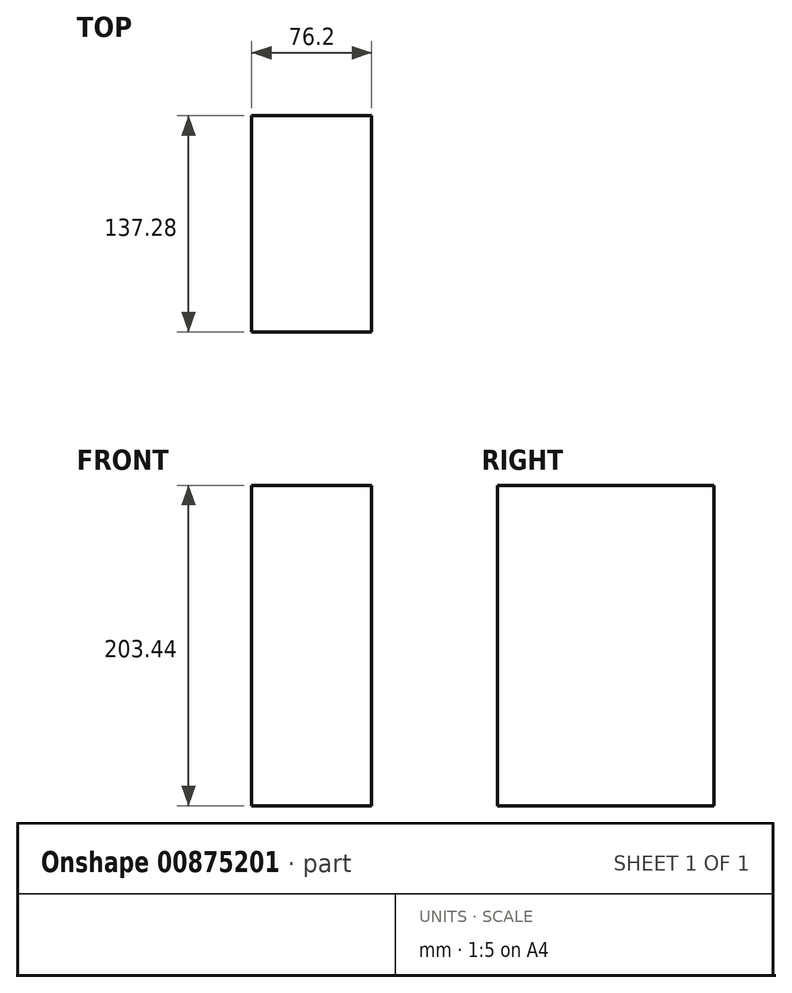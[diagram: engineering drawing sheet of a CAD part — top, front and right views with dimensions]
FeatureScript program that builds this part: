
annotation { "Feature Type Name" : "Feature", "Feature Type Description" : "" }
export const myFeature = defineFeature(function(context is Context, id is Id, definition is map)
    precondition{}
    {
        {
            var Q0;
            Q0=qCreatedBy(makeId("Right.planeOp"),FACE);
            var sketch = newSketch(context, id + "F0", { "sketchPlane" : qUnion([Q0])});
            skLineSegment(sketch, "E0.bottom", {"start": v(-68.64, 101.72) * mm, "end": v(68.64, 101.72) * mm});
            skLineSegment(sketch, "E0.top", {"start": v(-68.64, -101.72) * mm, "end": v(68.64, -101.72) * mm});
            skLineSegment(sketch, "E0.left", {"start": v(-68.64, 101.72) * mm, "end": v(-68.64, -101.72) * mm});
            skLineSegment(sketch, "E0.right", {"start": v(68.64, 101.72) * mm, "end": v(68.64, -101.72) * mm});
            skPoint(sketch, "E0.middle", {"position": v(0, 0) * mm});
            skSolve(sketch);
        }
        {
            var Q0;
            Q0=makeQuery(id+"F0.imprint","IMPRINT",FACE,{"disambiguationData":[TD([[makeQuery(id+"F0.imprint","IMPRINT",EDGE,{"derivedFrom":sQuery(id+"F0.wireOp",EDGE,"E0.bottom")}),-1.0]])]});
            extrude(context, id + "F1", {"entities" : qUnion([Q0]), "depth" : 76.2 * mm, "offsetDistance" : 25.4 * mm});
        }
    });
